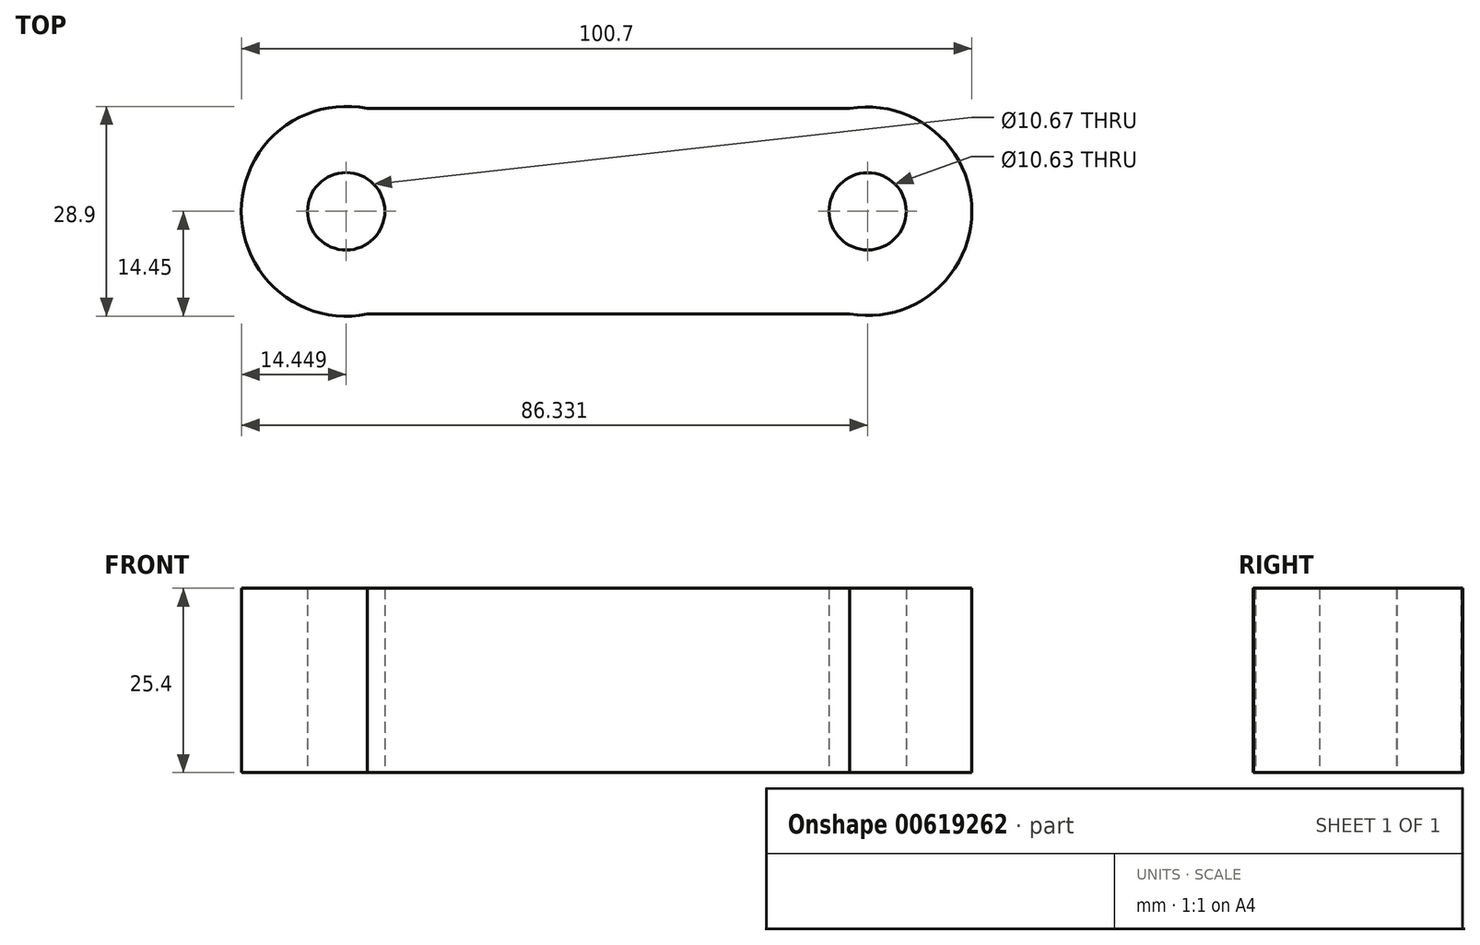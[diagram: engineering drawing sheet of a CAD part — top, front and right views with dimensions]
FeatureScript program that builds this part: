
annotation { "Feature Type Name" : "Feature", "Feature Type Description" : "" }
export const myFeature = defineFeature(function(context is Context, id is Id, definition is map)
    precondition{}
    {
        {
            var Q0;
            Q0=qCreatedBy(makeId("Top.planeOp"),FACE);
            var sketch = newSketch(context, id + "F0", { "sketchPlane" : qUnion([Q0])});
            skLineSegment(sketch, "E0.bottom", {"start": v(35.94, -14.16) * mm, "end": v(-35.94, -14.16) * mm});
            skLineSegment(sketch, "E0.top", {"start": v(35.94, 14.16) * mm, "end": v(-35.94, 14.16) * mm});
            skLineSegment(sketch, "E0.left", {"start": v(35.94, -14.16) * mm, "end": v(35.94, 14.16) * mm});
            skLineSegment(sketch, "E0.right", {"start": v(-35.94, -14.16) * mm, "end": v(-35.94, 14.16) * mm});
            skPoint(sketch, "E0.middle", {"position": v(0, 0) * mm});
            skCircle(sketch, "E1", {"center": v(-35.94, 0) * mm, "radius": 14.45 * mm});
            skCircle(sketch, "E2", {"center": v(35.94, 0) * mm, "radius": 14.37 * mm});
            skCircle(sketch, "E3", {"center": v(-35.94, 0) * mm, "radius": 5.33 * mm});
            skCircle(sketch, "E4", {"center": v(35.94, 0) * mm, "radius": 5.32 * mm});
            skLineSegment(sketch, "E5.bottom", {"start": v(18.92, -6.36) * mm, "end": v(-18.92, -6.36) * mm});
            skLineSegment(sketch, "E5.top", {"start": v(18.92, 6.36) * mm, "end": v(-18.92, 6.36) * mm});
            skLineSegment(sketch, "E5.left", {"start": v(18.92, -6.36) * mm, "end": v(18.92, 6.36) * mm});
            skLineSegment(sketch, "E5.right", {"start": v(-18.92, -6.36) * mm, "end": v(-18.92, 6.36) * mm});
            skSolve(sketch);
        }
        {
            var Q0;
            {var subQ0=sQuery(id+"F0.wireOp",EDGE,"E0.right");var subQ5=sQuery(id+"F0.wireOp",EDGE,"E0.bottom");var subQ6=makeQuery(id+"F0.imprint","INTERSECT",VERTEX,{"derivedFrom":[subQ5,subQ0]});Q0=makeQuery(id+"F0.imprint","IMPRINT",FACE,{"disambiguationData":[TD([[makeQuery(id+"F0.imprint","IMPRINT",EDGE,{"disambiguationData":[TD([[subQ6,1.0]])],"derivedFrom":subQ5}),-1.0]])]});}
            var Q1;
            {var subQ0=sQuery(id+"F0.wireOp",EDGE,"E0.right");var subQ5=sQuery(id+"F0.wireOp",EDGE,"E0.bottom");var subQ6=makeQuery(id+"F0.imprint","INTERSECT",VERTEX,{"derivedFrom":[subQ5,subQ0]});Q1=makeQuery(id+"F0.imprint","IMPRINT",FACE,{"disambiguationData":[TD([[makeQuery(id+"F0.imprint","IMPRINT",EDGE,{"disambiguationData":[TD([[subQ6,1.0]])],"derivedFrom":subQ5}),1.0]])]});}
            var Q2;
            Q2=makeQuery(id+"F0.imprint","IMPRINT",FACE,{"disambiguationData":[TD([[makeQuery(id+"F0.imprint","IMPRINT",EDGE,{"derivedFrom":sQuery(id+"F0.wireOp",EDGE,"E5.bottom")}),1.0]])]});
            var Q3;
            Q3=makeQuery(id+"F0.imprint","IMPRINT",FACE,{"disambiguationData":[TD([[makeQuery(id+"F0.imprint","IMPRINT",EDGE,{"derivedFrom":sQuery(id+"F0.wireOp",EDGE,"E5.bottom")}),-1.0]])]});
            var Q4;
            {var subQ0=sQuery(id+"F0.wireOp",EDGE,"E0.left");var subQ1=sQuery(id+"F0.wireOp",EDGE,"E0.bottom");var subQ2=makeQuery(id+"F0.imprint","INTERSECT",VERTEX,{"derivedFrom":[subQ1,subQ0]});Q4=makeQuery(id+"F0.imprint","IMPRINT",FACE,{"disambiguationData":[TD([[makeQuery(id+"F0.imprint","IMPRINT",EDGE,{"disambiguationData":[TD([[subQ2,-1.0]])],"derivedFrom":subQ1}),-1.0]])]});}
            var Q5;
            {var subQ0=sQuery(id+"F0.wireOp",EDGE,"E0.left");var subQ1=sQuery(id+"F0.wireOp",EDGE,"E0.bottom");var subQ2=makeQuery(id+"F0.imprint","INTERSECT",VERTEX,{"derivedFrom":[subQ1,subQ0]});Q5=makeQuery(id+"F0.imprint","IMPRINT",FACE,{"disambiguationData":[TD([[makeQuery(id+"F0.imprint","IMPRINT",EDGE,{"disambiguationData":[TD([[subQ2,-1.0]])],"derivedFrom":subQ1}),1.0]])]});}
            extrude(context, id + "F1", {"entities" : qUnion([Q0, Q1, Q2, Q3, Q4, Q5]), "depth" : 25.4 * mm, "offsetDistance" : 25.4 * mm});
        }
    });
